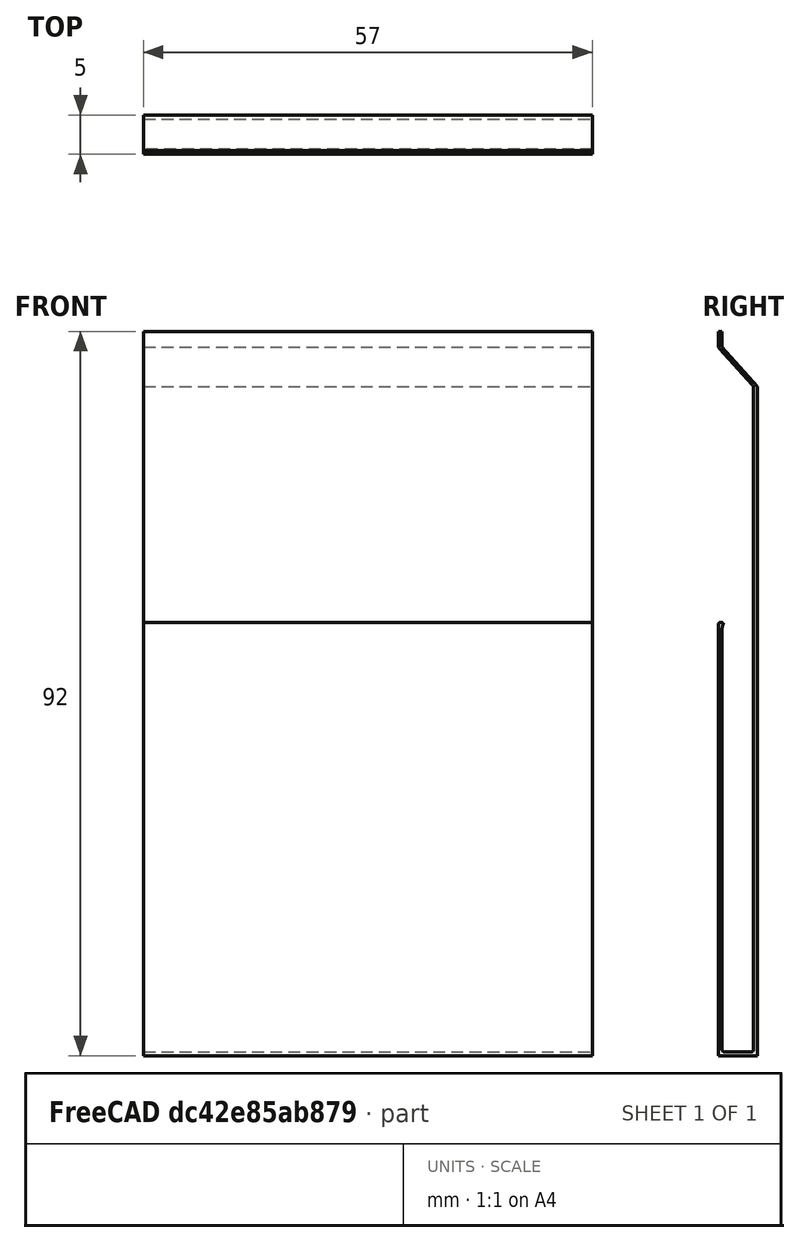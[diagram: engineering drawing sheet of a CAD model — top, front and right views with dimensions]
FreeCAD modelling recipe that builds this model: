
FCSTD DOCUMENT  (FreeCAD 0.20R29410 (Git))
Label: pocket
License: All rights reserved
LicenseURL: http://en.wikipedia.org/wiki/All_rights_reserved
objects: Sketcher::SketchObject×1, PartDesign::Pad×1, PartDesign::Body×1
note: 4 computed .brp shape members not serialized (recipe doc carries the construction recipe); baked Part::Feature solids carry a one-line shape summary decoded from their .brp

FEATURE [Sketcher::SketchObject] Sketch005
  FullyConstrained = true
  MapMode = 5
  Placement = pos=(0,0,0) rot=(0.57735,0.57735,0.57735;2.0944rad)
  Support = -> [YZ_Plane002]
  sketch-geometry (27):
    g0: LineSegment StartX=-10 StartY=10 StartZ=0 EndX=-15 EndY=10 EndZ=0
    g1: LineSegment StartX=-10 StartY=10 StartZ=0 EndX=-10 EndY=95 EndZ=0
    g2: LineSegment StartX=-15 StartY=10 StartZ=0 EndX=-15 EndY=64.8 EndZ=0
    g3: LineSegment StartX=-14.5 StartY=64.2615 StartZ=0 EndX=-14.5 EndY=10.75 EndZ=0
    g4: LineSegment StartX=-14.25 StartY=10.5 StartZ=0 EndX=-10.75 EndY=10.5 EndZ=0
    g5: LineSegment StartX=-10.5 StartY=10.75 StartZ=0 EndX=-10.5 EndY=94.75 EndZ=0
    g6: LineSegment StartX=-15 StartY=102 StartZ=0 EndX=-15 EndY=100.227 EndZ=0
    g7: LineSegment StartX=-15 StartY=102 StartZ=0 EndX=-14.5 EndY=102 EndZ=0
    g8: LineSegment StartX=-14.5 StartY=102 StartZ=0 EndX=-14.5 EndY=100 EndZ=0
    g9: LineSegment StartX=-14.5 StartY=100 StartZ=0 EndX=-10 EndY=95 EndZ=0
    g10: LineSegment StartX=-14.8483 StartY=99.8314 StartZ=0 EndX=-10.6672 EndY=95.1858 EndZ=0
    g11: LineSegment StartX=-14.8 StartY=65 StartZ=0 EndX=-14.5 EndY=65 EndZ=0
    g12: LineSegment StartX=-14.4114 StartY=64.7215 StartZ=0 EndX=-14.3743 EndY=64.8143 EndZ=0
    g13: ArcOfCircle CenterX=-14.5 CenterY=64.8646 CenterZ=0 NormalX=0 NormalY=0 NormalZ=1 AngleXU=0 Radius=0.135407 StartAngle=5.90268 EndAngle=7.85398
    g14: GeomPoint X=-14.3 Y=65 Z=0
    g15: ArcOfCircle CenterX=-14.8 CenterY=64.8 CenterZ=0 NormalX=0 NormalY=0 NormalZ=1 AngleXU=0 Radius=0.2 StartAngle=1.5708 EndAngle=3.14159
    g16: GeomPoint X=-15 Y=65 Z=0
    g17: ArcOfCircle CenterX=-13.2615 CenterY=64.2615 CenterZ=0 NormalX=0 NormalY=0 NormalZ=1 AngleXU=0 Radius=1.23852 StartAngle=2.76109 EndAngle=3.14159
    g18: GeomPoint X=-14.5 Y=64.5 Z=0
    g19: ArcOfCircle CenterX=-11.1515 CenterY=94.75 CenterZ=0 NormalX=0 NormalY=0 NormalZ=1 AngleXU=0 Radius=0.65149 StartAngle=-1.07e-14 EndAngle=0.732815
    g20: GeomPoint X=-10.5 Y=95 Z=0
    g21: ArcOfCircle CenterX=-14.4089 CenterY=100.227 CenterZ=0 NormalX=0 NormalY=0 NormalZ=1 AngleXU=0 Radius=0.591063 StartAngle=3.14159 EndAngle=3.87441
    g22: GeomPoint X=-15 Y=100 Z=0
    g23: ArcOfCircle CenterX=-14.25 CenterY=10.75 CenterZ=0 NormalX=0 NormalY=0 NormalZ=1 AngleXU=0 Radius=0.25 StartAngle=3.14159 EndAngle=4.71239
    g24: GeomPoint X=-14.5 Y=10.5 Z=0
    g25: ArcOfCircle CenterX=-10.75 CenterY=10.75 CenterZ=0 NormalX=0 NormalY=0 NormalZ=1 AngleXU=0 Radius=0.25 StartAngle=4.71239 EndAngle=6.28319
    g26: GeomPoint X=-10.5 Y=10.5 Z=0
  constraints (67):
    c: Horizontal(g0)
    c: DistanceX(g0,g0) = 5
    c: DistanceY(g-1,g0) = 10
    c: DistanceX(g0,g-1) = 10
    c: Coincident(g1,g0)
    c: Vertical(g1)
    c: DistanceY(g1,g1) = 85
    c: Coincident(g2,g0)
    c: Vertical(g2)
    c: DistanceY(g2,g16) = 55
    c: DistanceX(g16,g18) = 0.5
    c: Vertical(g3)
    c: DistanceY(g0,g24) = 0.5
    c: Horizontal(g4)
    c: DistanceX(g26,g0) = 0.5
    c: Vertical(g5)
    c: DistanceY(g26,g20) = 84.5
    c: Vertical(g6)
    c: DistanceY(g22,g6) = 2
    c: Coincident(g7,g6)
    c: Horizontal(g7)
    c: DistanceX(g7,g7) = 0.5
    c: Coincident(g8,g7)
    c: Vertical(g8)
    c: DistanceY(g8,g8) = 2
    c: DistanceX(g22,g1) = 5
    c: Coincident(g9,g8)
    c: Coincident(g9,g1)
    c: DistanceY(g1,g8) = 5
    c: DistanceY(g24,g18) = 54
    c: Horizontal(g11)
    c: DistanceX(g16,g14) = 0.7
    c: PointOnObject(g14,g11)
    c: PointOnObject(g14,g12)
    c: Tangent(g11,g13) = 1.5708
    c: Tangent(g12,g13) = -1.5708
    c: PointOnObject(g16,g2)
    c: PointOnObject(g16,g11)
    c: Tangent(g2,g15) = 1.5708
    c: Tangent(g11,g15) = 1.5708
    c: PointOnObject(g18,g3)
    c: PointOnObject(g18,g12)
    c: Tangent(g3,g17) = -1.5708
    c: Tangent(g12,g17) = 1.5708
    c: Vertical(g3,g11)
    c: DistanceX(g11,g11) = 0.3
    c: Distance(g12) = 0.1
    c: PointOnObject(g20,g5)
    c: PointOnObject(g20,g10)
    c: Tangent(g5,g19) = -1.5708
    c: Tangent(g10,g19) = 1.5708
    c: PointOnObject(g22,g6)
    c: PointOnObject(g22,g10)
    c: Tangent(g6,g21) = -1.5708
    c: Tangent(g10,g21) = -1.5708
    c: PointOnObject(g24,g3)
    c: PointOnObject(g24,g4)
    c: Tangent(g3,g23) = -1.5708
    c: Tangent(g4,g23) = -1.5708
    c: PointOnObject(g26,g4)
    c: PointOnObject(g26,g5)
    c: Tangent(g4,g25) = -1.5708
    c: Tangent(g5,g25) = -1.5708
    c: DistanceX(g4,g4) = 3.5
    c: Horizontal(g5,g3)
    c: DistanceY(g5,g5) = 84
    c: Distance(g10) = 6.25
FEATURE [PartDesign::Pad] Pad002
  Direction = (1,-2e-16,3e-16)
  Length = 57
  Length2 = 10
  Placement = pos=(0,0,0) rot=(0.57735,0.57735,0.57735;2.0944rad)
  Profile = -> Sketch005
  ReferenceAxis = -> Sketch005 [N_Axis]
  Type = 0
FEATURE [PartDesign::Body] Body002  label="pocket"
  Group = -> [Sketch005,Pad002]
  Origin = -> Origin002
  Tip = -> Pad002
